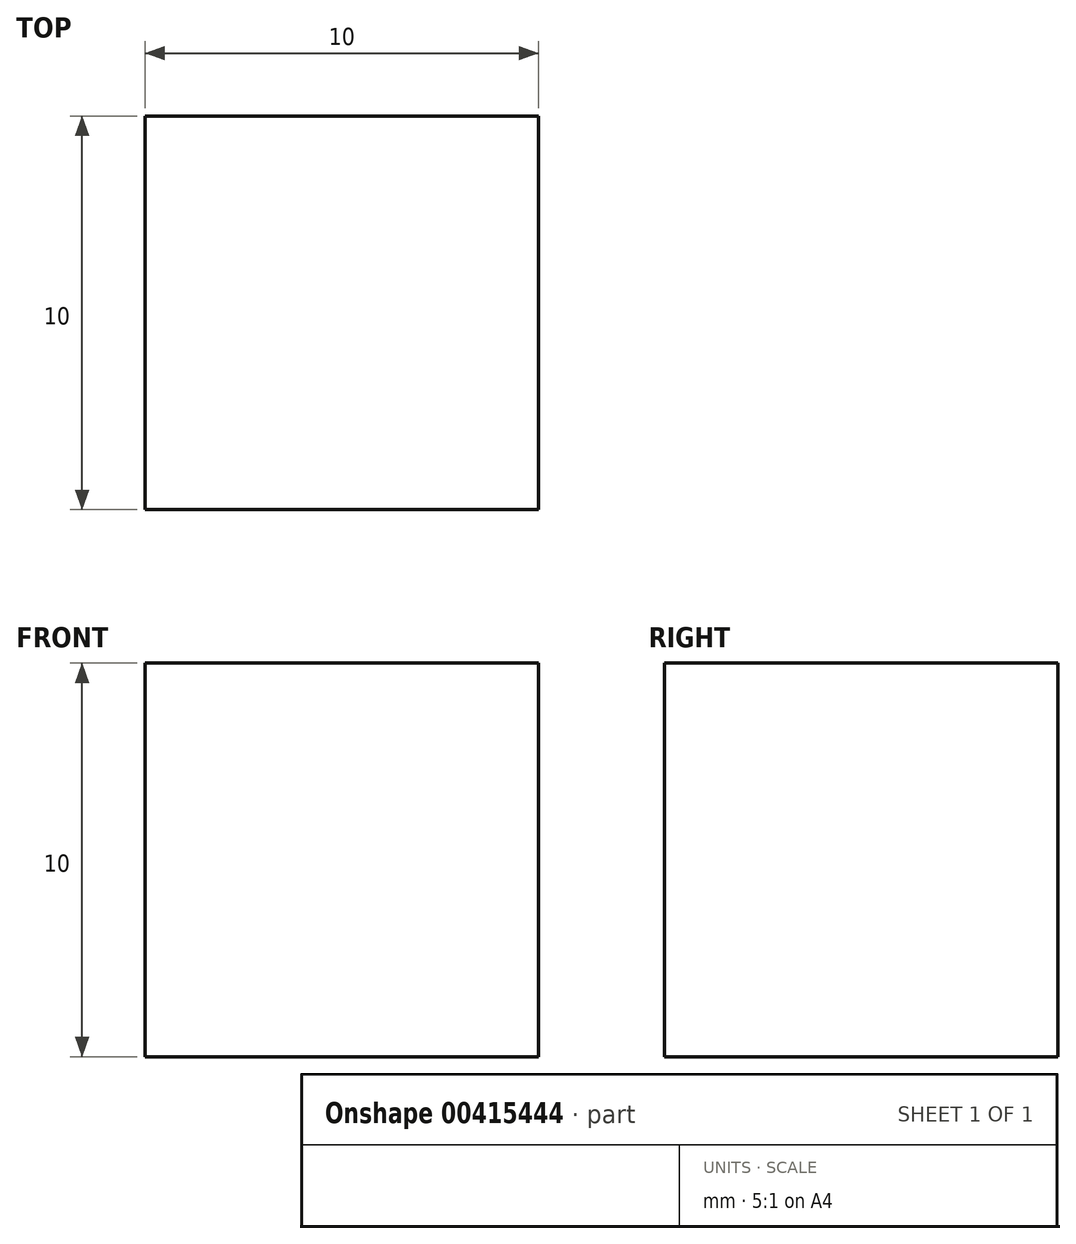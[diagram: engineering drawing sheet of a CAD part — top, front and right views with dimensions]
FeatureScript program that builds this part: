
annotation { "Feature Type Name" : "Feature", "Feature Type Description" : "" }
export const myFeature = defineFeature(function(context is Context, id is Id, definition is map)
    precondition{}
    {
        {
            var Q0;
            Q0=qCreatedBy(makeId("Top.planeOp"),FACE);
            var sketch = newSketch(context, id + "F0", { "sketchPlane" : qUnion([Q0])});
            skLineSegment(sketch, "E0.bottom", {"start": v(-24.69, 15.97) * mm, "end": v(-14.69, 15.97) * mm});
            skLineSegment(sketch, "E0.top", {"start": v(-24.69, 25.97) * mm, "end": v(-14.69, 25.97) * mm});
            skLineSegment(sketch, "E0.left", {"start": v(-24.69, 15.97) * mm, "end": v(-24.69, 25.97) * mm});
            skLineSegment(sketch, "E0.right", {"start": v(-14.69, 15.97) * mm, "end": v(-14.69, 25.97) * mm});
            skSolve(sketch);
        }
        {
            var Q0;
            Q0 = qSketchRegion(id + "F0", true);
            extrude(context, id + "F1", {"entities" : qUnion([Q0]), "depth" : 10 * mm});
        }
    });
